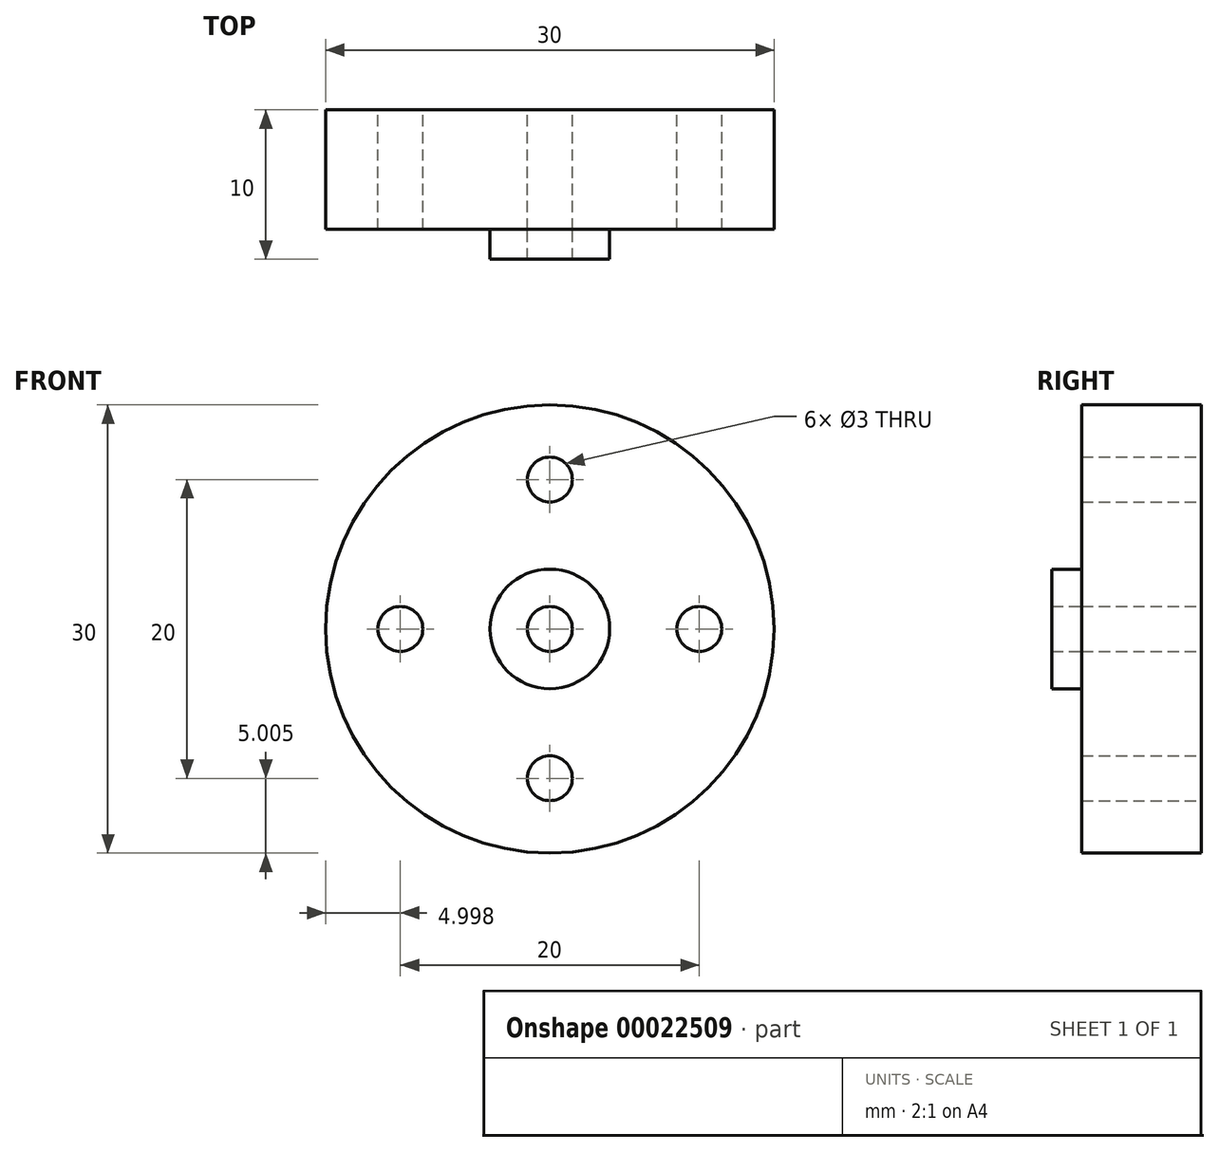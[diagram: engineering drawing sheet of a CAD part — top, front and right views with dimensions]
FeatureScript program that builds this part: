
annotation { "Feature Type Name" : "Feature", "Feature Type Description" : "" }
export const myFeature = defineFeature(function(context is Context, id is Id, definition is map)
    precondition{}
    {
        {
            var Q0;
            Q0=qCreatedBy(makeId("Front.planeOp"),FACE);
            var sketch = newSketch(context, id + "F0", { "sketchPlane" : qUnion([Q0])});
            skCircle(sketch, "E0", {"center": v(-32.3, 19.44) * mm, "radius": 15 * mm});
            skCircle(sketch, "E1", {"center": v(-32.3, 19.44) * mm, "radius": 1.5 * mm});
            skCircle(sketch, "E2", {"center": v(-32.3, 29.44) * mm, "radius": 1.5 * mm});
            skCircle(sketch, "E3.1.0", {"center": v(-42.3, 19.44) * mm, "radius": 1.5 * mm});
            skCircle(sketch, "E3.2.0", {"center": v(-32.3, 9.44) * mm, "radius": 1.5 * mm});
            skCircle(sketch, "E3.3.0", {"center": v(-22.3, 19.44) * mm, "radius": 1.5 * mm});
            skSolve(sketch);
        }
        {
            var Q0;
            Q0=qSketchRegion(id+"F0",true);
            extrude(context, id + "F1", {"entities" : qUnion([Q0]), "depth" : 3 * mm});
        }
        {
            var Q0;
            Q0=makeQuery(id+"F1.opExtrude","CAP_FACE",FACE,{"disambiguationData":[OSD([sQuery(id+"F0.wireOp",EDGE,"E0"),sQuery(id+"F0.wireOp",EDGE,"E1"),sQuery(id+"F0.wireOp",EDGE,"E2"),sQuery(id+"F0.wireOp",EDGE,"E3.1.0"),sQuery(id+"F0.wireOp",EDGE,"E3.2.0"),sQuery(id+"F0.wireOp",EDGE,"E3.3.0")])],"isStart":false});
            var sketch = newSketch(context, id + "F2", { "sketchPlane" : qUnion([Q0])});
            skCircle(sketch, "E4", {"center": v(-32.3, 19.44) * mm, "radius": 13 * mm});
            skSolve(sketch);
        }
        {
            var Q0;
            Q0=makeQuery(id+"F2.imprint","IMPRINT",FACE,{"disambiguationData":[TD([[makeQuery(id+"F2.imprint","IMPRINT",EDGE,{"derivedFrom":sQuery(id+"F2.wireOp",EDGE,"E4")}),1.0]])]});
            var Q1;
            Q1=makeQuery(id+"F2.imprint","IMPRINT",FACE,{"disambiguationData":[TD([[makeQuery(id+"F2.imprint","IMPRINT",EDGE,{"derivedFrom":sQuery(id+"F2.wireOp",EDGE,"E4")}),-1.0]])]});
            extrude(context, id + "F3", {"entities" : qUnion([Q0, Q1]), "operationType" : NewBodyOperationType.ADD, "depth" : 5 * mm});
        }
        {
            var Q0;
            Q0=makeQuery(id+"F3.opExtrude","CAP_FACE",FACE,{"disambiguationData":[OSD([sQuery(id+"F0.wireOp",EDGE,"E0"),sQuery(id+"F0.wireOp",EDGE,"E1"),sQuery(id+"F0.wireOp",EDGE,"E2"),sQuery(id+"F0.wireOp",EDGE,"E3.1.0"),sQuery(id+"F0.wireOp",EDGE,"E3.2.0"),sQuery(id+"F0.wireOp",EDGE,"E3.3.0")])],"isStart":false});
            var sketch = newSketch(context, id + "F4", { "sketchPlane" : qUnion([Q0])});
            skCircle(sketch, "E5", {"center": v(-32.3, 19.44) * mm, "radius": 4 * mm});
            skSolve(sketch);
        }
        {
            var Q0;
            Q0=makeQuery(id+"F4.imprint","IMPRINT",FACE,{"disambiguationData":[TD([[makeQuery(id+"F4.imprint","IMPRINT",EDGE,{"derivedFrom":sQuery(id+"F4.wireOp",EDGE,"E5")}),1.0]])]});
            extrude(context, id + "F5", {"entities" : qUnion([Q0]), "depth" : 2 * mm});
        }
    });
